# Revit family: Lighting-Recessed-Luminii-Glint-Hero
name_source: partatom
category: Lighting Fixtures
units: mm (PartAtom-declared; Revit-internal decimal feet)

## family parameters
Cut with Voids When Loaded = No
Host = Face
Light Source = No
OmniClass Number = 23.80.70.11.14.11
OmniClass Title = Downlights
Part Type = Normal
Room Calculation Point = No
Round Connector Dimension = Use Diameter
Shared = No

## types (1)
- Recessed
    Apparent Load = 0 VA
    Assembly Code = D5020200
    Cable Finish = Aluminum - Luminii - White
    Default Elevation = 48.0000"
    Description = Lightshift Adjustable Luminaire
    Fixture Height = 3.0000"
    Host Width = 13.7520"
    Housing Finish = Aluminum - Luminii - White
    Keynote = 16510
    Lens Finish = Acrylic - Luminii - Frosted
    Manufacturer = Luminii
    Model = Hero Recessed
    Product ID = SFFL
    Trim Finish = Aluminum - Luminii - Black
    URL = https://www.luminii.com
    Voltage = 120 V
    Wattage = 23 W
    Width = 1.7520"

## geometry (parser evidence)
native form markers: Sweep x24
no freeform markers — native parametric forms only
